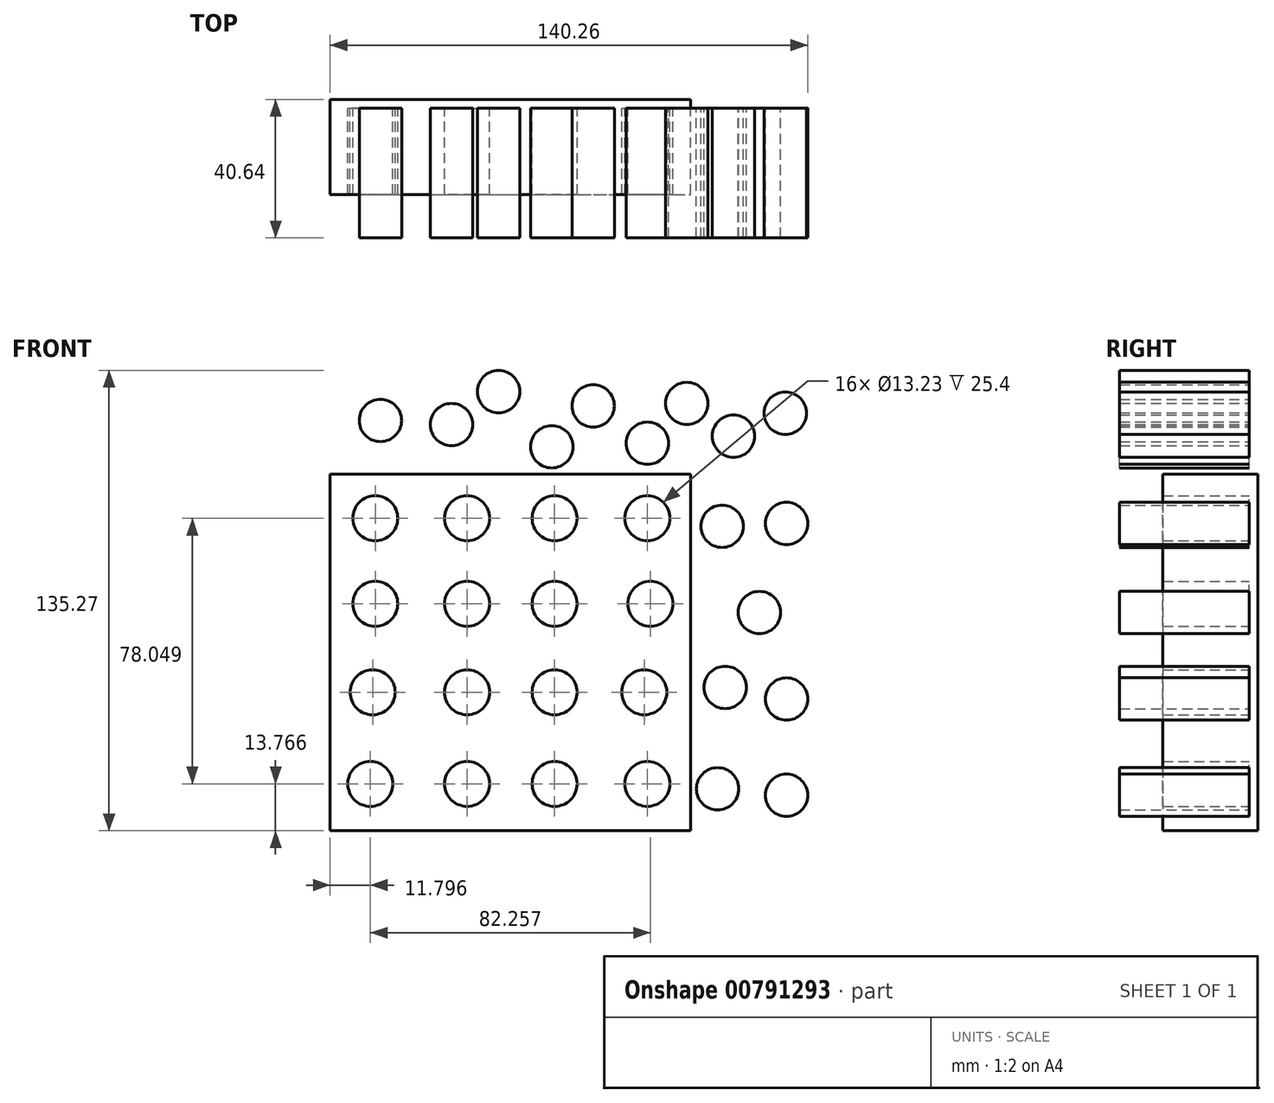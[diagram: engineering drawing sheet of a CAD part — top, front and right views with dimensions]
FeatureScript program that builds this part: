
annotation { "Feature Type Name" : "Feature", "Feature Type Description" : "" }
export const myFeature = defineFeature(function(context is Context, id is Id, definition is map)
    precondition{}
    {
        {
            var Q0;
            Q0=qCreatedBy(makeId("Front.planeOp"),FACE);
            var sketch = newSketch(context, id + "F0", { "sketchPlane" : qUnion([Q0])});
            skLineSegment(sketch, "E0.bottom", {"start": v(-73.03, 46.26) * mm, "end": v(32.83, 46.26) * mm});
            skLineSegment(sketch, "E0.top", {"start": v(-73.03, -58.54) * mm, "end": v(32.83, -58.54) * mm});
            skLineSegment(sketch, "E0.left", {"start": v(-73.03, 46.26) * mm, "end": v(-73.03, -58.54) * mm});
            skLineSegment(sketch, "E0.right", {"start": v(32.83, 46.26) * mm, "end": v(32.83, -58.54) * mm});
            skLineSegment(sketch, "E1", {"start": v(-46.56, 46.26) * mm, "end": v(-46.56, -58.54) * mm});
            skLineSegment(sketch, "E2", {"start": v(-20.1, 46.26) * mm, "end": v(-20.1, -58.54) * mm});
            skLineSegment(sketch, "E3", {"start": v(6.37, 46.26) * mm, "end": v(6.37, -58.54) * mm});
            skLineSegment(sketch, "E4", {"start": v(-73.03, 20.86) * mm, "end": v(32.83, 20.86) * mm});
            skLineSegment(sketch, "E5", {"start": v(-73.03, -5.6) * mm, "end": v(32.83, -5.6) * mm});
            skLineSegment(sketch, "E6", {"start": v(-73.03, -32.07) * mm, "end": v(32.83, -32.07) * mm});
            skCircle(sketch, "E7", {"center": v(-59.8, 33.27) * mm, "radius": 6.62 * mm});
            skCircle(sketch, "E8", {"center": v(-59.8, 8.16) * mm, "radius": 6.62 * mm});
            skCircle(sketch, "E9", {"center": v(-61.23, -44.77) * mm, "radius": 6.62 * mm});
            skCircle(sketch, "E10", {"center": v(-60.57, -17.85) * mm, "radius": 6.62 * mm});
            skCircle(sketch, "E11", {"center": v(-32.8, 33.27) * mm, "radius": 6.62 * mm});
            skCircle(sketch, "E12", {"center": v(-32.8, 8.16) * mm, "radius": 6.62 * mm});
            skCircle(sketch, "E13", {"center": v(-32.8, -17.85) * mm, "radius": 6.62 * mm});
            skCircle(sketch, "E14", {"center": v(-32.8, -44.77) * mm, "radius": 6.62 * mm});
            skCircle(sketch, "E15", {"center": v(-7.1, 33.27) * mm, "radius": 6.62 * mm});
            skCircle(sketch, "E16", {"center": v(-7.1, 8.16) * mm, "radius": 6.62 * mm});
            skCircle(sketch, "E17", {"center": v(-7.1, -17.85) * mm, "radius": 6.62 * mm});
            skCircle(sketch, "E18", {"center": v(-7.1, -44.77) * mm, "radius": 6.62 * mm});
            skCircle(sketch, "E19", {"center": v(20.12, 33.27) * mm, "radius": 6.62 * mm});
            skCircle(sketch, "E20", {"center": v(21.02, 8.16) * mm, "radius": 6.62 * mm});
            skCircle(sketch, "E21", {"center": v(19.2, -17.85) * mm, "radius": 6.62 * mm});
            skCircle(sketch, "E22", {"center": v(20.12, -44.77) * mm, "radius": 6.62 * mm});
            skSolve(sketch);
        }
        {
            var Q0;
            Q0=makeQuery(id+"F0.imprint","IMPRINT",FACE,{"disambiguationData":[TD([[makeQuery(id+"F0.imprint","IMPRINT",EDGE,{"derivedFrom":sQuery(id+"F0.wireOp",EDGE,"f6cMR4RI-uvaH-WxtC-Ak8X-GHSHe8VUsqIl")}),1.0]])]});
            var Q1;
            Q1=makeQuery(id+"F0.imprint","IMPRINT",FACE,{"disambiguationData":[TD([[makeQuery(id+"F0.imprint","IMPRINT",EDGE,{"derivedFrom":sQuery(id+"F0.wireOp",EDGE,"beI59wNb-htPK-Epvf-uCSg-h64YHkvHfvWi")}),1.0]])]});
            var Q2;
            Q2=makeQuery(id+"F0.imprint","IMPRINT",FACE,{"disambiguationData":[TD([[makeQuery(id+"F0.imprint","IMPRINT",EDGE,{"derivedFrom":sQuery(id+"F0.wireOp",EDGE,"Ro4P9Jne-YRZA-ghka-mF0Z-Gw1Lloqhbgse")}),1.0]])]});
            var Q3;
            Q3=makeQuery(id+"F0.imprint","IMPRINT",FACE,{"disambiguationData":[TD([[makeQuery(id+"F0.imprint","IMPRINT",EDGE,{"derivedFrom":sQuery(id+"F0.wireOp",EDGE,"a7DnQpmL-hSie-FLp3-kmJH-OdSJdfs0Ju8X")}),1.0]])]});
            var Q4;
            Q4=makeQuery(id+"F0.imprint","IMPRINT",FACE,{"disambiguationData":[TD([[makeQuery(id+"F0.imprint","IMPRINT",EDGE,{"derivedFrom":sQuery(id+"F0.wireOp",EDGE,"LQSFjD4u-mKKw-7PxX-t05z-Kf5JEXamwdQJ")}),1.0]])]});
            var Q5;
            Q5=makeQuery(id+"F0.imprint","IMPRINT",FACE,{"disambiguationData":[TD([[makeQuery(id+"F0.imprint","IMPRINT",EDGE,{"derivedFrom":sQuery(id+"F0.wireOp",EDGE,"487XH686-HmCU-XHsT-BKaq-aCNQauaAiQbR")}),1.0]])]});
            var Q6;
            Q6=makeQuery(id+"F0.imprint","IMPRINT",FACE,{"disambiguationData":[TD([[makeQuery(id+"F0.imprint","IMPRINT",EDGE,{"derivedFrom":sQuery(id+"F0.wireOp",EDGE,"IMCXvL4H-oCtV-Hxhk-zr0I-DIEBXSzwtxDm")}),1.0]])]});
            var Q7;
            Q7=makeQuery(id+"F0.imprint","IMPRINT",FACE,{"disambiguationData":[TD([[makeQuery(id+"F0.imprint","IMPRINT",EDGE,{"derivedFrom":sQuery(id+"F0.wireOp",EDGE,"J8XFENO7-CQLL-JKKP-Bxkp-PXAzSnpSG6MX")}),1.0]])]});
            var Q8;
            Q8=makeQuery(id+"F0.imprint","IMPRINT",FACE,{"disambiguationData":[TD([[makeQuery(id+"F0.imprint","IMPRINT",EDGE,{"derivedFrom":sQuery(id+"F0.wireOp",EDGE,"DeUDxIwN-rfOt-d7dh-kJS3-4t5n3aSNQYM6")}),1.0]])]});
            var Q9;
            Q9=makeQuery(id+"F0.imprint","IMPRINT",FACE,{"disambiguationData":[TD([[makeQuery(id+"F0.imprint","IMPRINT",EDGE,{"derivedFrom":sQuery(id+"F0.wireOp",EDGE,"diVVqVv2-gFMy-7LnB-3iXJ-aNHNxAK2nCzw")}),1.0]])]});
            var Q10;
            Q10=makeQuery(id+"F0.imprint","IMPRINT",FACE,{"disambiguationData":[TD([[makeQuery(id+"F0.imprint","IMPRINT",EDGE,{"derivedFrom":sQuery(id+"F0.wireOp",EDGE,"XGlcriWh-waLc-Czha-q0D4-Ji0hQn8kSOkl")}),1.0]])]});
            var Q11;
            Q11=makeQuery(id+"F0.imprint","IMPRINT",FACE,{"disambiguationData":[TD([[makeQuery(id+"F0.imprint","IMPRINT",EDGE,{"derivedFrom":sQuery(id+"F0.wireOp",EDGE,"95ktKKX3-0gLg-6PeB-9Xqe-t6mbwVnDXgGR")}),1.0]])]});
            var Q12;
            Q12=makeQuery(id+"F0.imprint","IMPRINT",FACE,{"disambiguationData":[TD([[makeQuery(id+"F0.imprint","IMPRINT",EDGE,{"derivedFrom":sQuery(id+"F0.wireOp",EDGE,"It15ayi7-uzjr-vzFx-GhxX-IjPEs1hWf7OF")}),1.0]])]});
            var Q13;
            Q13=makeQuery(id+"F0.imprint","IMPRINT",FACE,{"disambiguationData":[TD([[makeQuery(id+"F0.imprint","IMPRINT",EDGE,{"derivedFrom":sQuery(id+"F0.wireOp",EDGE,"E7")}),-1.0]])]});
            var Q14;
            Q14=makeQuery(id+"F0.imprint","IMPRINT",FACE,{"disambiguationData":[TD([[makeQuery(id+"F0.imprint","IMPRINT",EDGE,{"derivedFrom":sQuery(id+"F0.wireOp",EDGE,"E19")}),-1.0]])]});
            var Q15;
            Q15=makeQuery(id+"F0.imprint","IMPRINT",FACE,{"disambiguationData":[TD([[makeQuery(id+"F0.imprint","IMPRINT",EDGE,{"derivedFrom":sQuery(id+"F0.wireOp",EDGE,"E9")}),-1.0]])]});
            var Q16;
            Q16=makeQuery(id+"F0.imprint","IMPRINT",FACE,{"disambiguationData":[TD([[makeQuery(id+"F0.imprint","IMPRINT",EDGE,{"derivedFrom":sQuery(id+"F0.wireOp",EDGE,"E22")}),-1.0]])]});
            var Q17;
            Q17=makeQuery(id+"F0.imprint","IMPRINT",FACE,{"disambiguationData":[TD([[makeQuery(id+"F0.imprint","IMPRINT",EDGE,{"derivedFrom":sQuery(id+"F0.wireOp",EDGE,"E15")}),-1.0]])]});
            var Q18;
            Q18=makeQuery(id+"F0.imprint","IMPRINT",FACE,{"disambiguationData":[TD([[makeQuery(id+"F0.imprint","IMPRINT",EDGE,{"derivedFrom":sQuery(id+"F0.wireOp",EDGE,"E14")}),-1.0]])]});
            var Q19;
            Q19=makeQuery(id+"F0.imprint","IMPRINT",FACE,{"disambiguationData":[TD([[makeQuery(id+"F0.imprint","IMPRINT",EDGE,{"derivedFrom":sQuery(id+"F0.wireOp",EDGE,"E18")}),-1.0]])]});
            var Q20;
            Q20=makeQuery(id+"F0.imprint","IMPRINT",FACE,{"disambiguationData":[TD([[makeQuery(id+"F0.imprint","IMPRINT",EDGE,{"derivedFrom":sQuery(id+"F0.wireOp",EDGE,"E8")}),-1.0]])]});
            var Q21;
            Q21=makeQuery(id+"F0.imprint","IMPRINT",FACE,{"disambiguationData":[TD([[makeQuery(id+"F0.imprint","IMPRINT",EDGE,{"derivedFrom":sQuery(id+"F0.wireOp",EDGE,"E10")}),-1.0]])]});
            var Q22;
            Q22=makeQuery(id+"F0.imprint","IMPRINT",FACE,{"disambiguationData":[TD([[makeQuery(id+"F0.imprint","IMPRINT",EDGE,{"derivedFrom":sQuery(id+"F0.wireOp",EDGE,"E20")}),-1.0]])]});
            var Q23;
            Q23=makeQuery(id+"F0.imprint","IMPRINT",FACE,{"disambiguationData":[TD([[makeQuery(id+"F0.imprint","IMPRINT",EDGE,{"derivedFrom":sQuery(id+"F0.wireOp",EDGE,"E21")}),-1.0]])]});
            var Q24;
            Q24=makeQuery(id+"F0.imprint","IMPRINT",FACE,{"disambiguationData":[TD([[makeQuery(id+"F0.imprint","IMPRINT",EDGE,{"derivedFrom":sQuery(id+"F0.wireOp",EDGE,"E12")}),-1.0]])]});
            var Q25;
            Q25=makeQuery(id+"F0.imprint","IMPRINT",FACE,{"disambiguationData":[TD([[makeQuery(id+"F0.imprint","IMPRINT",EDGE,{"derivedFrom":sQuery(id+"F0.wireOp",EDGE,"E16")}),-1.0]])]});
            var Q26;
            Q26=makeQuery(id+"F0.imprint","IMPRINT",FACE,{"disambiguationData":[TD([[makeQuery(id+"F0.imprint","IMPRINT",EDGE,{"derivedFrom":sQuery(id+"F0.wireOp",EDGE,"E17")}),-1.0]])]});
            var Q27;
            Q27=makeQuery(id+"F0.imprint","IMPRINT",FACE,{"disambiguationData":[TD([[makeQuery(id+"F0.imprint","IMPRINT",EDGE,{"derivedFrom":sQuery(id+"F0.wireOp",EDGE,"E13")}),-1.0]])]});
            var Q28;
            Q28=makeQuery(id+"F0.imprint","IMPRINT",FACE,{"disambiguationData":[TD([[makeQuery(id+"F0.imprint","IMPRINT",EDGE,{"derivedFrom":sQuery(id+"F0.wireOp",EDGE,"nJOtrbzP-sjic-m2ei-vCUI-ohxY2OJvO1Hr")}),1.0]])]});
            var Q29;
            Q29=makeQuery(id+"F0.imprint","IMPRINT",FACE,{"disambiguationData":[TD([[makeQuery(id+"F0.imprint","IMPRINT",EDGE,{"derivedFrom":sQuery(id+"F0.wireOp",EDGE,"bvP3HOtH-lKWV-W53q-uxcP-Ft61FSrnAh5L")}),1.0]])]});
            var Q30;
            Q30=makeQuery(id+"F0.imprint","IMPRINT",FACE,{"disambiguationData":[TD([[makeQuery(id+"F0.imprint","IMPRINT",EDGE,{"derivedFrom":sQuery(id+"F0.wireOp",EDGE,"E11")}),-1.0]])]});
            var Q31;
            Q31=makeQuery(id+"F0.imprint","IMPRINT",FACE,{"disambiguationData":[TD([[makeQuery(id+"F0.imprint","IMPRINT",EDGE,{"derivedFrom":sQuery(id+"F0.wireOp",EDGE,"J04EwLim-atUO-OtrB-h5Jn-5Vfk33Sd6PMb")}),1.0]])]});
            extrude(context, id + "F1", {"entities" : qUnion([Q0, Q1, Q2, Q3, Q4, Q5, Q6, Q7, Q8, Q9, Q10, Q11, Q12, Q13, Q14, Q15, Q16, Q17, Q18, Q19, Q20, Q21, Q22, Q23, Q24, Q25, Q26, Q27, Q28, Q29, Q30, Q31]), "depth" : 25.4 * mm, "offsetDistance" : 25.4 * mm});
        }
        {
            var Q0;
            Q0=makeQuery(id+"F1.opExtrude","CAP_FACE",FACE,{"disambiguationData":[OSD([sQuery(id+"F0.wireOp",EDGE,"E0.bottom"),sQuery(id+"F0.wireOp",EDGE,"E0.top"),sQuery(id+"F0.wireOp",EDGE,"E0.left"),sQuery(id+"F0.wireOp",EDGE,"E0.right"),sQuery(id+"F0.wireOp",EDGE,"E7"),sQuery(id+"F0.wireOp",EDGE,"E8"),sQuery(id+"F0.wireOp",EDGE,"E9"),sQuery(id+"F0.wireOp",EDGE,"E10"),sQuery(id+"F0.wireOp",EDGE,"E11"),sQuery(id+"F0.wireOp",EDGE,"E12"),sQuery(id+"F0.wireOp",EDGE,"E13"),sQuery(id+"F0.wireOp",EDGE,"E14"),sQuery(id+"F0.wireOp",EDGE,"E15"),sQuery(id+"F0.wireOp",EDGE,"E16"),sQuery(id+"F0.wireOp",EDGE,"E17"),sQuery(id+"F0.wireOp",EDGE,"E18"),sQuery(id+"F0.wireOp",EDGE,"E19"),sQuery(id+"F0.wireOp",EDGE,"E20"),sQuery(id+"F0.wireOp",EDGE,"E21"),sQuery(id+"F0.wireOp",EDGE,"E22")])],"isStart":true});
            var sketch = newSketch(context, id + "F2", { "sketchPlane" : qUnion([Q0])});
            skLineSegment(sketch, "E23.bottom", {"start": v(-32.83, 46.26) * mm, "end": v(73.03, 46.26) * mm});
            skLineSegment(sketch, "E23.top", {"start": v(-32.83, -58.54) * mm, "end": v(73.03, -58.54) * mm});
            skLineSegment(sketch, "E23.left", {"start": v(-32.83, 46.26) * mm, "end": v(-32.83, -58.54) * mm});
            skLineSegment(sketch, "E23.right", {"start": v(73.03, 46.26) * mm, "end": v(73.03, -58.54) * mm});
            skSolve(sketch);
        }
        {
            var Q0;
            Q0 = qSketchRegion(id + "F2", true);
            extrude(context, id + "F3", {"entities" : qUnion([Q0]), "operationType" : NewBodyOperationType.ADD, "depth" : 2.54 * mm, "offsetDistance" : 25.4 * mm});
        }
        {
            var Q0;
            Q0=qCreatedBy(makeId("Front.planeOp"),FACE);
            var sketch = newSketch(context, id + "F4", { "sketchPlane" : qUnion([Q0])});
            skCircle(sketch, "E24", {"center": v(-58.27, 62.04) * mm, "radius": 6.22 * mm});
            skCircle(sketch, "E25", {"center": v(-37.4, 60.82) * mm, "radius": 6.22 * mm});
            skCircle(sketch, "E26", {"center": v(-23.57, 70.5) * mm, "radius": 6.22 * mm});
            skCircle(sketch, "E27", {"center": v(-7.94, 54.3) * mm, "radius": 6.22 * mm});
            skCircle(sketch, "E28", {"center": v(4.21, 66.33) * mm, "radius": 6.22 * mm});
            skCircle(sketch, "E29", {"center": v(20.16, 55.34) * mm, "radius": 6.22 * mm});
            skCircle(sketch, "E30", {"center": v(31.72, 67.04) * mm, "radius": 6.22 * mm});
            skCircle(sketch, "E31", {"center": v(45.43, 57.44) * mm, "radius": 6.22 * mm});
            skCircle(sketch, "E32", {"center": v(60.65, 64.15) * mm, "radius": 6.22 * mm});
            skCircle(sketch, "E33", {"center": v(42.08, 30.93) * mm, "radius": 6.22 * mm});
            skCircle(sketch, "E34", {"center": v(61.01, 31.74) * mm, "radius": 6.22 * mm});
            skCircle(sketch, "E35", {"center": v(53.05, 5.58) * mm, "radius": 6.22 * mm});
            skCircle(sketch, "E36", {"center": v(43, -16.43) * mm, "radius": 6.22 * mm});
            skCircle(sketch, "E37", {"center": v(61.01, -19.84) * mm, "radius": 6.22 * mm});
            skCircle(sketch, "E38", {"center": v(40.77, -46.24) * mm, "radius": 6.22 * mm});
            skCircle(sketch, "E39", {"center": v(61.01, -48.14) * mm, "radius": 6.22 * mm});
            skSolve(sketch);
        }
        {
            var Q0;
            Q0 = qSketchRegion(id + "F4", true);
            extrude(context, id + "F5", {"entities" : qUnion([Q0]), "depth" : 38.1 * mm, "offsetDistance" : 25.4 * mm});
        }
    });
